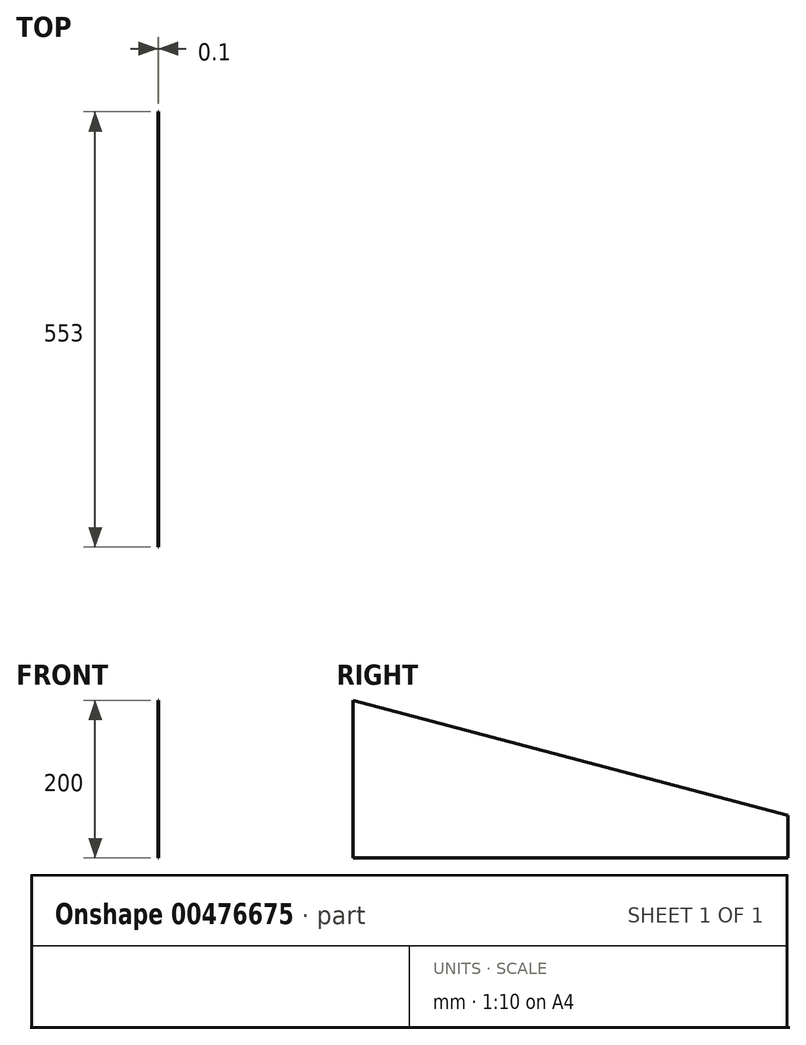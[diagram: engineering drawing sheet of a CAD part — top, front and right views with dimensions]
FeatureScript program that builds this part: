
annotation { "Feature Type Name" : "Feature", "Feature Type Description" : "" }
export const myFeature = defineFeature(function(context is Context, id is Id, definition is map)
    precondition{}
    {
        {
            var Q0;
            Q0=qCreatedBy(makeId("Right.planeOp"),FACE);
            var sketch = newSketch(context, id + "F0", { "sketchPlane" : qUnion([Q0])});
            skLineSegment(sketch, "E0", {"start": v(0, 0) * mm, "end": v(0, 54) * mm});
            skLineSegment(sketch, "E1", {"start": v(0, 54) * mm, "end": v(-553, 200) * mm});
            skLineSegment(sketch, "E2", {"start": v(-553, 200) * mm, "end": v(-553, 0) * mm});
            skLineSegment(sketch, "E3", {"start": v(-553, 0) * mm, "end": v(0, 0) * mm});
            skSolve(sketch);
        }
        {
            var Q0;
            Q0 = qSketchRegion(id + "F0", true);
            extrude(context, id + "F1", {"entities" : qUnion([Q0]), "depth" : 0.1 * mm});
        }
    });
